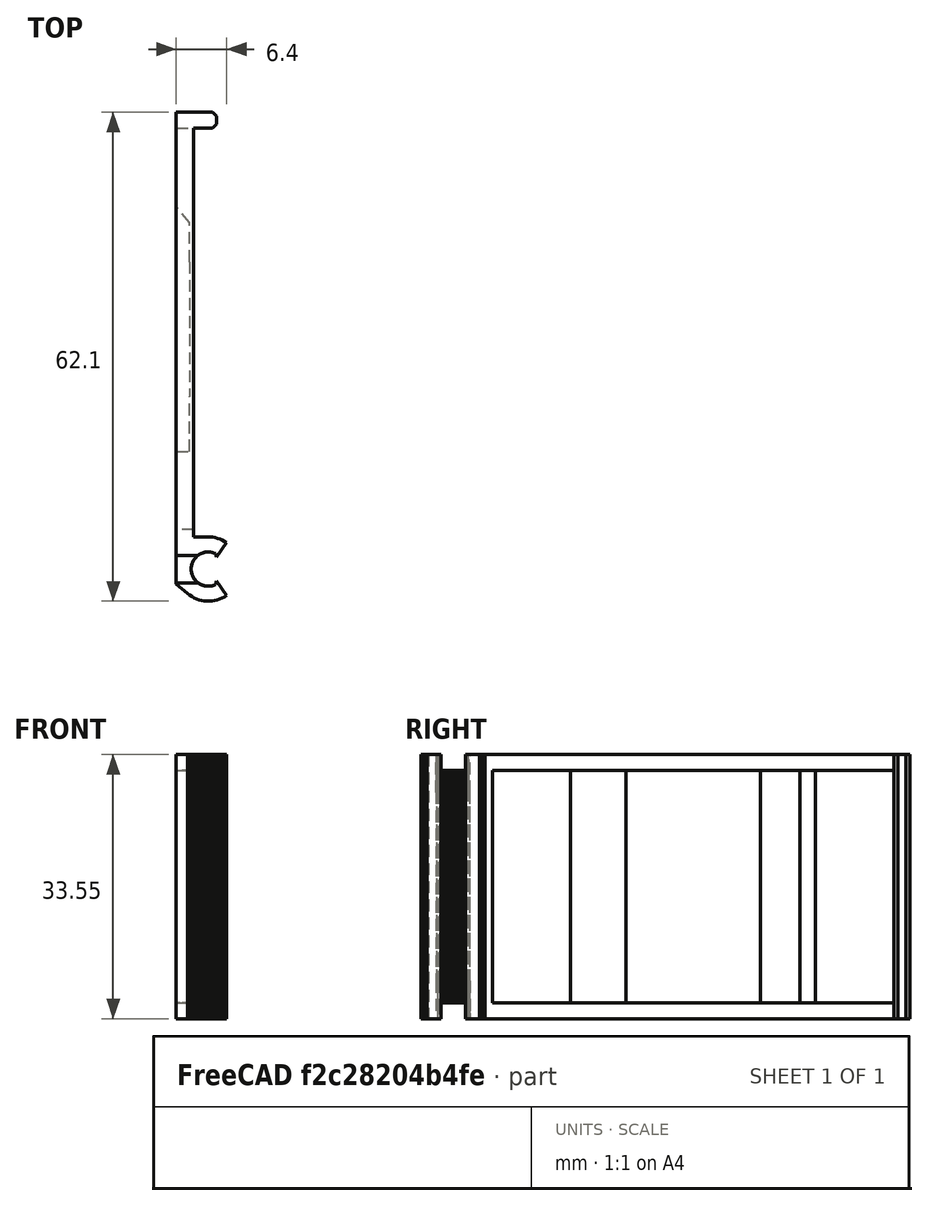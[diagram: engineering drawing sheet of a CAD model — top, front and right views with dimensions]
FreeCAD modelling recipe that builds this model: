
FCSTD DOCUMENT  (FreeCAD 0.19R23463 (Git))
Label: bottom
License: All rights reserved
LicenseURL: http://en.wikipedia.org/wiki/All_rights_reserved
objects: Part::Feature×1, Part::Refine×1, Mesh::Feature×1, PartDesign::FeatureBase×1, PartDesign::Plane×1, Sketcher::SketchObject×1, PartDesign::Pad×1, PartDesign::Body×1
note: 8 computed .brp shape members not serialized (recipe doc carries the construction recipe); baked Part::Feature solids carry a one-line shape summary decoded from their .brp

FEATURE [Part::Feature] bottom_and_hinge_3001_solid  label="bottom_and_hinge_3001 (Solid)"
  shape: bbox 6.4 x 62.1 x 33.55 mm, 960 faces (baked)
FEATURE [Part::Refine] bottom_and_hinge_3001_solid001  label="bottom_and_hinge_3001 (Solid)001"
  Source = -> bottom_and_hinge_3001_solid
FEATURE [Mesh::Feature] bottom_and_hinge_3
FEATURE [PartDesign::FeatureBase] BaseFeature
  BaseFeature = -> bottom_and_hinge_3001_solid001
FEATURE [PartDesign::Plane] DatumPlane
  Length = 96.9693
  MapMode = 5
  Placement = pos=(-4.075,0,0) rot=(0.57735,-0.57735,-0.57735;2.0944rad)
  ResizeMode = 0
  Support = -> [BaseFeature]
  Width = 72.4943
FEATURE [Sketcher::SketchObject] Sketch
  ExternalGeometry = -> [BaseFeature]
  MapMode = 5
  Placement = pos=(-4.075,0,0) rot=(0.57735,-0.57735,-0.57735;2.0944rad)
  Support = -> [DatumPlane]
  sketch-geometry (4):
    g0: LineSegment StartX=-39.025 StartY=31.55 StartZ=0 EndX=-21.925 EndY=31.55 EndZ=0
    g1: LineSegment StartX=-21.925 StartY=31.55 StartZ=0 EndX=-21.925 EndY=2 EndZ=0
    g2: LineSegment StartX=-21.925 StartY=2 StartZ=0 EndX=-39.025 EndY=2 EndZ=0
    g3: LineSegment StartX=-39.025 StartY=2 StartZ=0 EndX=-39.025 EndY=31.55 EndZ=0
  constraints (10):
    c: Coincident(g0,g1)
    c: Coincident(g1,g2)
    c: Coincident(g2,g3)
    c: Coincident(g3,g0)
    c: Horizontal(g0)
    c: Horizontal(g2)
    c: Vertical(g1)
    c: Vertical(g3)
    c: Coincident(g0,g-5)
    c: Coincident(g1,g-6)
FEATURE [PartDesign::Pad] Pad
  BaseFeature = -> BaseFeature
  Direction = (1,1,1)
  Length = 1.72
  Length2 = 100
  Profile = -> Sketch
  Reversed = true
  Type = 0
FEATURE [PartDesign::Body] Body
  BaseFeature = -> bottom_and_hinge_3001_solid001
  Group = -> [BaseFeature,DatumPlane,Sketch,Pad]
  Origin = -> Origin
  Tip = -> Pad
